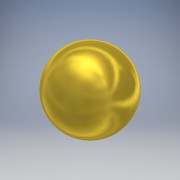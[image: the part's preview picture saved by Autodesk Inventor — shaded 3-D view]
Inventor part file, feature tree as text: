
AUTODESK INVENTOR PART (.ipt)
format: ipt  version: 2018 (Build 220112000, 112)  size: 124,928 bytes
history: native  units: mm
features: revolve x1, sketch x1
ambient origin geometry x8: Origin, YZ Plane, XZ Plane, XY Plane, X Axis, Y Axis, Z Axis, Center Point
bodies: Solid1 (feature_tree)
feature tree (2):
  revolve  "Revolution1"  Angle=90.0deg
  sketch  "Sketch1"  dims[d0=24.0mm d1=90.0deg]
